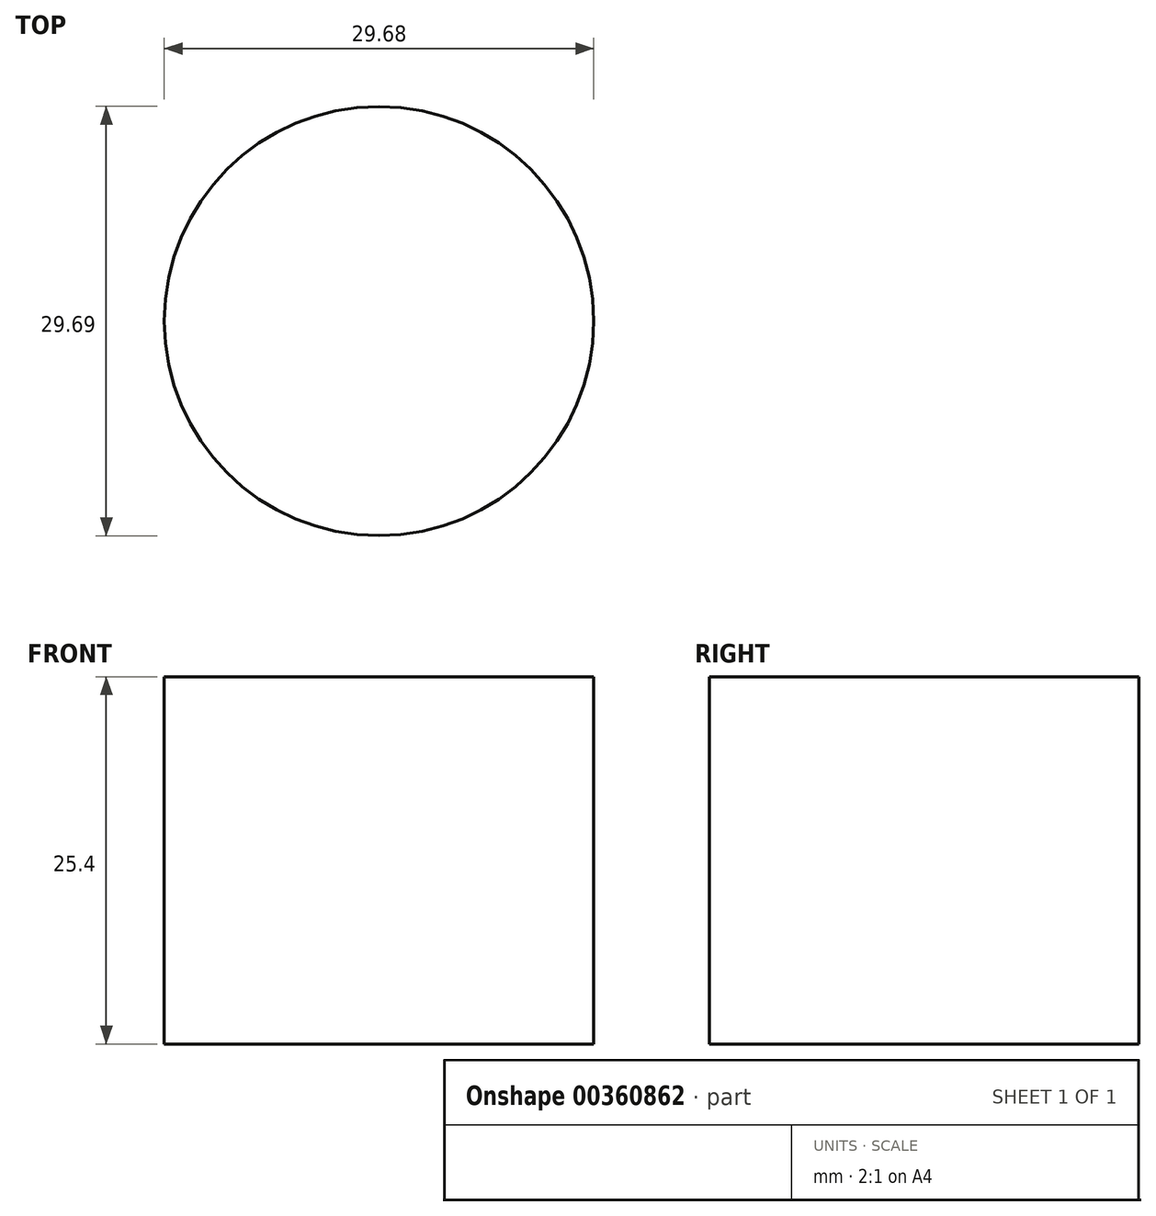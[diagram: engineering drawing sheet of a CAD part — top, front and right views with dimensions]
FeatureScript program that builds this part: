
annotation { "Feature Type Name" : "Feature", "Feature Type Description" : "" }
export const myFeature = defineFeature(function(context is Context, id is Id, definition is map)
    precondition{}
    {
        {
            var Q0;
            Q0=qCreatedBy(makeId("Top.planeOp"),FACE);
            var sketch = newSketch(context, id + "F0", { "sketchPlane" : qUnion([Q0])});
            skCircle(sketch, "E0", {"center": v(-133.65, 21.71) * mm, "radius": 14.84 * mm});
            skSolve(sketch);
        }
        {
            var Q0;
            Q0 = qSketchRegion(id + "F0", true);
            extrude(context, id + "F1", {"entities" : qUnion([Q0]), "depth" : 25.4 * mm});
        }
    });
